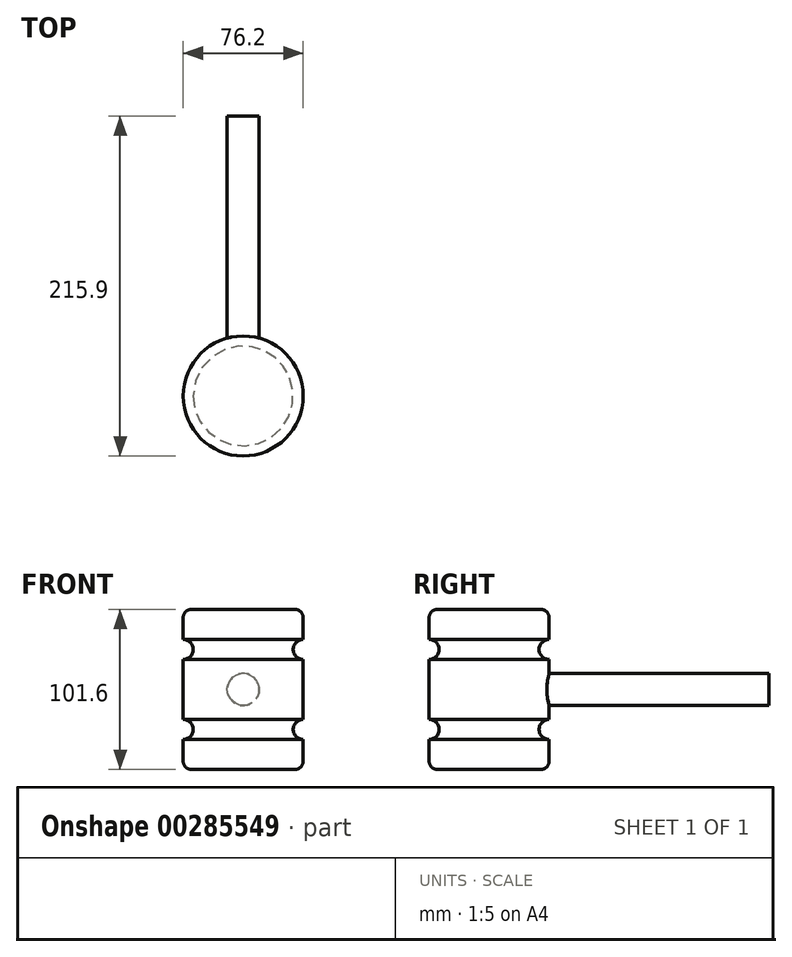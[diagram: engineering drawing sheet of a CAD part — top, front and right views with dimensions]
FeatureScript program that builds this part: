
annotation { "Feature Type Name" : "Feature", "Feature Type Description" : "" }
export const myFeature = defineFeature(function(context is Context, id is Id, definition is map)
    precondition{}
    {
        {
            var Q0;
            Q0=qCreatedBy(makeId("Front.planeOp"),FACE);
            var sketch = newSketch(context, id + "F0", { "sketchPlane" : qUnion([Q0])});
            skLineSegment(sketch, "E0.bottom", {"start": v(0, 0) * mm, "end": v(-38.1, 0) * mm});
            skLineSegment(sketch, "E0.top", {"start": v(0, 101.6) * mm, "end": v(-38.1, 101.6) * mm});
            skLineSegment(sketch, "E0.left", {"start": v(0, 0) * mm, "end": v(0, 19.05) * mm});
            skLineSegment(sketch, "E0.right", {"start": v(-38.1, 0) * mm, "end": v(-38.1, 101.6) * mm});
            skArc(sketch, "E1", {"start": v(0, 82.55) * mm, "mid": v(-6.35, 76.2) * mm, "end": v(0, 69.85) * mm});
            skArc(sketch, "E2", {"start": v(0, 31.75) * mm, "mid": v(-6.35, 25.4) * mm, "end": v(0, 19.05) * mm});
            skLineSegment(sketch, "E3.trimOffspring", {"start": v(0, 31.75) * mm, "end": v(0, 69.85) * mm});
            skLineSegment(sketch, "E4.trimOffspring", {"start": v(0, 82.55) * mm, "end": v(0, 101.6) * mm});
            skSolve(sketch);
        }
        {
            var Q0;
            Q0 = qSketchRegion(id + "F0", true);
            var Q1;
            Q1=sQuery(id+"F0.wireOp",EDGE,"E0.right");
            revolve(context, id + "F1", {"entities" : qUnion([Q0]), "axis" : qUnion([Q1]), "revolveType" : RevolveType.FULL});
        }
        {
            var Q0;
            Q0=makeQuery(id+"F1.opRevolve","SWEPT_EDGE",EDGE,{"disambiguationData":[OSD([sQuery(id+"F0.wireOp",EDGE,"E0.top"),sQuery(id+"F0.wireOp",EDGE,"E4.trimOffspring")])]});
            var Q1;
            Q1=makeQuery(id+"F1.opRevolve","SWEPT_EDGE",EDGE,{"disambiguationData":[OSD([sQuery(id+"F0.wireOp",EDGE,"E0.bottom"),sQuery(id+"F0.wireOp",EDGE,"E0.left")])]});
            fillet(context, id + "F2", {"entities" : qUnion([Q0, Q1]), "radius" : 5.08 * mm, "tangentPropagation" : true, "allowEdgeOverflow" : false});
        }
        {
            var Q0;
            Q0=qCreatedBy(makeId("Front.planeOp"),FACE);
            var sketch = newSketch(context, id + "F3", { "sketchPlane" : qUnion([Q0])});
            skCircle(sketch, "E5", {"center": v(-38.1, 50.8) * mm, "radius": 10.16 * mm});
            skSolve(sketch);
        }
        {
            var Q0;
            Q0 = qSketchRegion(id + "F3", true);
            extrude(context, id + "F4", {"entities" : qUnion([Q0]), "operationType" : NewBodyOperationType.REMOVE, "oppositeDirection" : true, "depth" : 152.4 * mm});
        }
        {
            var Q0;
            Q0=makeQuery(id+"F4.boolean.opBoolean","COPY",FACE,{"derivedFrom":makeQuery(id+"F4.opExtrude","CAP_FACE",FACE,{"disambiguationData":[OSD([sQuery(id+"F3.wireOp",EDGE,"E5")])],"isStart":true})});
            extrude(context, id + "F5", {"entities" : qUnion([Q0]), "operationType" : NewBodyOperationType.ADD, "depth" : 177.8 * mm});
        }
    });
